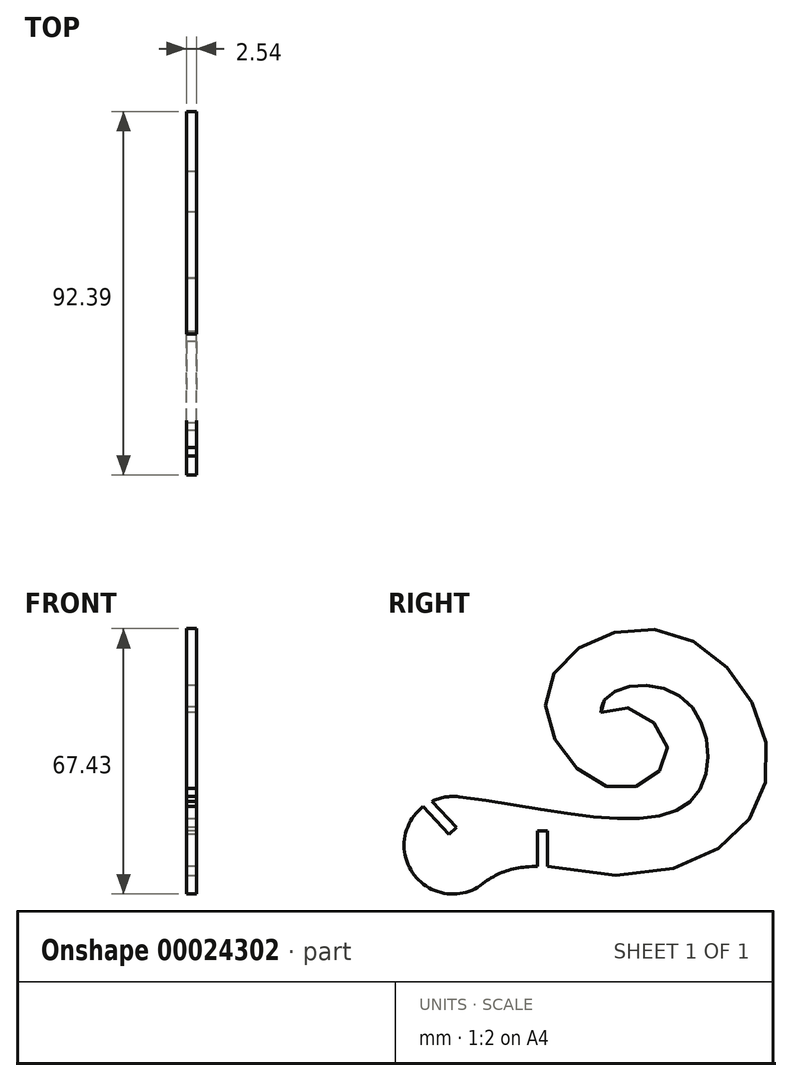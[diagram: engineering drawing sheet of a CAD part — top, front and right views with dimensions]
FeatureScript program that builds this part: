
annotation { "Feature Type Name" : "Feature", "Feature Type Description" : "" }
export const myFeature = defineFeature(function(context is Context, id is Id, definition is map)
    precondition{}
    {
        {
            var Q0;
            Q0=qCreatedBy(makeId("Right.planeOp"),FACE);
            var sketch = newSketch(context, id + "F0", { "sketchPlane" : qUnion([Q0])});
            skLineSegment(sketch, "E0", {"start": v(36.65, 0) * mm, "end": v(36.65, 8.94) * mm, "construction": true});
            skLineSegment(sketch, "E1", {"start": v(35.38, 8.94) * mm, "end": v(37.92, 8.94) * mm});
            skLineSegment(sketch, "E2", {"start": v(35.38, 8.94) * mm, "end": v(35.38, 0) * mm});
            skLineSegment(sketch, "E3", {"start": v(37.92, 8.94) * mm, "end": v(37.92, 0) * mm});
            skLineSegment(sketch, "E4", {"start": v(37.92, 8.94) * mm, "end": v(-10.34, 8.94) * mm, "construction": true});
            skLineSegment(sketch, "E5.bottom", {"start": v(13.79, 8.94) * mm, "end": v(1.09, 8.94) * mm, "construction": true});
            skLineSegment(sketch, "E5.top", {"start": v(13.79, 22.6) * mm, "end": v(1.09, 22.6) * mm, "construction": true});
            skLineSegment(sketch, "E5.left", {"start": v(13.79, 8.94) * mm, "end": v(13.79, 22.6) * mm, "construction": true});
            skLineSegment(sketch, "E5.right", {"start": v(1.09, 8.94) * mm, "end": v(1.09, 22.6) * mm, "construction": true});
            skLineSegment(sketch, "E6", {"start": v(1.09, 22.6) * mm, "end": v(13.79, 8.94) * mm, "construction": true});
            skLineSegment(sketch, "E7", {"start": v(14.72, 9.8) * mm, "end": v(12.86, 8.08) * mm});
            skLineSegment(sketch, "E8", {"start": v(14.72, 9.8) * mm, "end": v(8.49, 16.5) * mm});
            skLineSegment(sketch, "E9", {"start": v(12.86, 8.08) * mm, "end": v(6.28, 15.14) * mm});
            skPoint(sketch, "E10.visualSharp", {"position": v(4.8, 10.36) * mm});
            skPoint(sketch, "E11.visualSharp", {"position": v(13.25, 0) * mm});
            skPoint(sketch, "E12.trimOffspring.0.internal.orphan", {"position": v(0, 0) * mm});
            skPoint(sketch, "E13.visualSharp", {"position": v(0, -5.13) * mm});
            skPoint(sketch, "E14.startDerivative.orphan", {"position": v(0, 41.82) * mm});
            skPoint(sketch, "E15", {"position": v(35.38, 0) * mm});
            skPoint(sketch, "E16.orphan", {"position": v(11.78, 0) * mm});
            skArc(sketch, "E17", {"start": v(6.28, 15.14) * mm, "mid": v(20.35, -5.23) * mm, "end": v(8.49, 16.5) * mm});
            skFitSpline(sketch, "E18", {"points": [v(15.38, 17.63) * mm, v(74.63, 16.94) * mm, v(71.32, 43.42) * mm, v(51.52, 39.09) * mm], "startDerivative": vector(156.72, -19.43) * mm, "endDerivative": vector(2.74, -81.98) * mm});
            skFitSpline(sketch, "E19", {"points": [v(51.52, 39.09) * mm, v(68.25, 30.88) * mm, v(55.3, 19.79) * mm, v(37.56, 43.89) * mm, v(68.07, 59.7) * mm, v(93.69, 23.62) * mm, v(37.92, 0) * mm], "startDerivative": vector(130.13, 105.35) * mm, "endDerivative": vector(-431.04, 105.53) * mm});
            skFitSpline(sketch, "E20", {"points": [v(35.38, 0) * mm, v(21.52, -4.42) * mm], "startDerivative": vector(-17.75, -0.51) * mm, "endDerivative": vector(-11.79, -9.27) * mm});
            skLineSegment(sketch, "E21", {"start": v(36.65, 8.94) * mm, "end": v(36.65, 14.35) * mm, "construction": true});
            skLineSegment(sketch, "E22", {"start": v(8.49, 16.5) * mm, "end": v(6.28, 15.14) * mm, "construction": true});
            skLineSegment(sketch, "E23", {"start": v(7.44, 15.77) * mm, "end": v(24.42, -2.5) * mm, "construction": true});
            skSolve(sketch);
        }
        {
            var Q0;
            Q0 = qSketchRegion(id + "F0", true);
            extrude(context, id + "F1", {"entities" : qUnion([Q0]), "depth" : 2.54 * mm});
        }
    });
